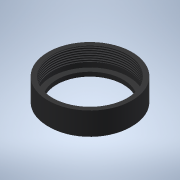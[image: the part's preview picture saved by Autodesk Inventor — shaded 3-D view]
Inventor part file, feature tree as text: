
AUTODESK INVENTOR PART (.ipt)
format: ipt  version: 2020.2 (Build 242310000, 310)  size: 169,472 bytes
history: native  units: mm
features: sketch x5, hole x3, extrude x2, plane x2, thread x1, chamfer x1
ambient origin geometry x8: Origin, YZ Plane, XZ Plane, XY Plane, X Axis, Y Axis, Z Axis, Center Point
bodies: Volumenkörper1 (feature_tree)
feature tree (14):
  extrude  "Extrusion1"  Depth=17.0mm TaperAngle=0.0deg
  hole  "Bohrung1"  [1 undecoded]
  plane  "Arbeitsebene1"
  plane  "Arbeitsebene2"
  extrude  "Extrusion4"  Depth=55.0mm
  hole  "Bohrung2"  [1 undecoded]
  thread  "Gewinde3"  [1 undecoded]
  chamfer  "Fase4"  Distance=23.75mm
  hole  "Bohrung3"  [1 undecoded]
  sketch  "Skizze2"  dims[d0=60.0mm d1=17.0mm d2=0.0mm]
  sketch  "Skizze6"  dims[d49=10.0mm d50=10.0mm d5=47.5mm d6=6.0mm d7=4.0mm d8=2.0mm d9=90.0deg d10=8.0mm d11=20.594885mm d31=-3.0mm]
  sketch  "Skizze7"  dims[d32=-7.0mm d34=55.0mm]
  sketch  "Skizze8"  dims[d35=2.0mm d36=0.0mm]
  sketch  "Skizze9"  dims[d37=53.5mm d38=6.0mm d39=4.0mm d40=2.0mm d41=90.0deg d42=10.0mm d43=20.594885mm d44=10.0mm d45=0.0mm d46=1.0mm d47=2.0mm d48=45.0deg d51=23.75mm d52=6.0mm d53=6.0mm d54=4.0mm d55=2.0mm d56=90.0deg d57=8.0mm d58=20.594885mm]
note: 4 required parameter values undecoded (feature->parameter linkage not recoverable at this tier; creation-order binding heuristic only, values carry confidence <= 0.55)
